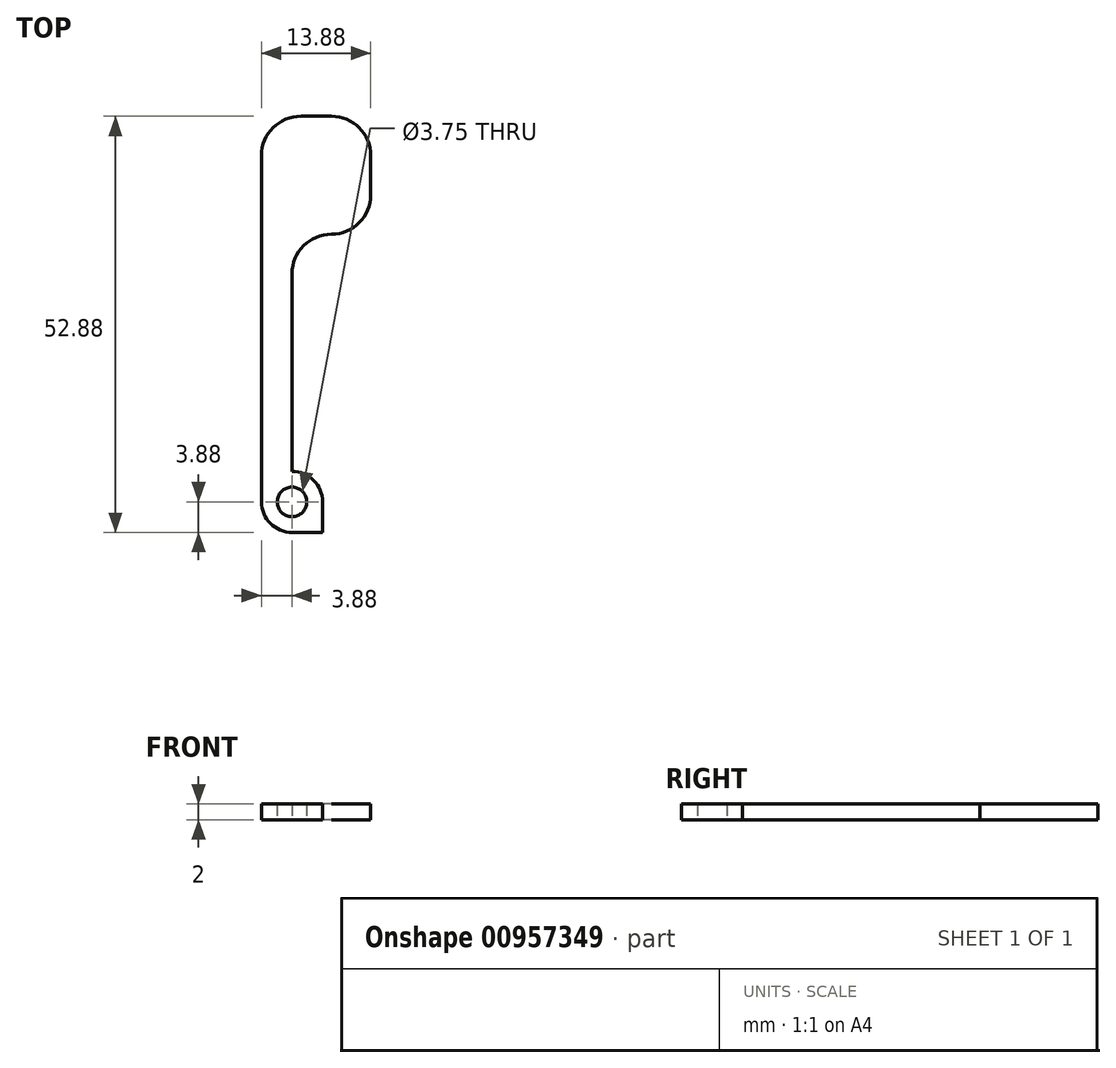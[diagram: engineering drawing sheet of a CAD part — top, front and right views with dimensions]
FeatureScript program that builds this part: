
annotation { "Feature Type Name" : "Feature", "Feature Type Description" : "" }
export const myFeature = defineFeature(function(context is Context, id is Id, definition is map)
    precondition{}
    {
        {
            var Q0;
            Q0=qCreatedBy(makeId("Top.planeOp"),FACE);
            var sketch = newSketch(context, id + "F0", { "sketchPlane" : qUnion([Q0])});
            skCircle(sketch, "E0", {"center": v(0, 0) * mm, "radius": 1.88 * mm});
            skArc(sketch, "E1", {"start": v(-3.88, 0) * mm, "mid": v(-2.74, -2.74) * mm, "end": v(0, -3.88) * mm});
            skLineSegment(sketch, "E2", {"start": v(0, -3.88) * mm, "end": v(3.88, -3.88) * mm});
            skLineSegment(sketch, "E3", {"start": v(3.88, -4.15) * mm, "end": v(3.88, -3.88) * mm});
            skLineSegment(sketch, "E4", {"start": v(0, 3.88) * mm, "end": v(0, 34) * mm});
            skLineSegment(sketch, "E5", {"start": v(0, 34) * mm, "end": v(10, 34) * mm});
            skLineSegment(sketch, "E6", {"start": v(10, 34) * mm, "end": v(10, 49) * mm});
            skLineSegment(sketch, "E7", {"start": v(10, 49) * mm, "end": v(-3.88, 49) * mm});
            skLineSegment(sketch, "E8", {"start": v(-3.88, 49) * mm, "end": v(-3.88, 0) * mm});
            skCircle(sketch, "E9", {"center": v(0, 0) * mm, "radius": 3.88 * mm});
            skLineSegment(sketch, "E10", {"start": v(3.88, -3.88) * mm, "end": v(3.88, 0) * mm});
            skSolve(sketch);
        }
        {
            var Q0;
            Q0 = qSketchRegion(id + "F0", true);
            extrude(context, id + "F1", {"entities" : qUnion([Q0]), "depth" : 2 * mm, "offsetDistance" : 25 * mm});
        }
        {
            var Q0;
            Q0=makeQuery(id+"F1.opExtrude","SWEPT_EDGE",EDGE,{"disambiguationData":[OSD([sQuery(id+"F0.wireOp",EDGE,"E4"),sQuery(id+"F0.wireOp",EDGE,"E5")])]});
            var Q1;
            Q1=makeQuery(id+"F1.opExtrude","SWEPT_EDGE",EDGE,{"disambiguationData":[OSD([sQuery(id+"F0.wireOp",EDGE,"E5"),sQuery(id+"F0.wireOp",EDGE,"E6")])]});
            var Q2;
            Q2=makeQuery(id+"F1.opExtrude","SWEPT_EDGE",EDGE,{"disambiguationData":[OSD([sQuery(id+"F0.wireOp",EDGE,"E6"),sQuery(id+"F0.wireOp",EDGE,"E7")])]});
            var Q3;
            Q3=makeQuery(id+"F1.opExtrude","SWEPT_EDGE",EDGE,{"disambiguationData":[OSD([sQuery(id+"F0.wireOp",EDGE,"E7"),sQuery(id+"F0.wireOp",EDGE,"E8")])]});
            fillet(context, id + "F2", {"entities" : qUnion([Q0, Q1, Q2, Q3]), "radius" : 5 * mm, "tangentPropagation" : true, "allowEdgeOverflow" : false});
        }
    });
